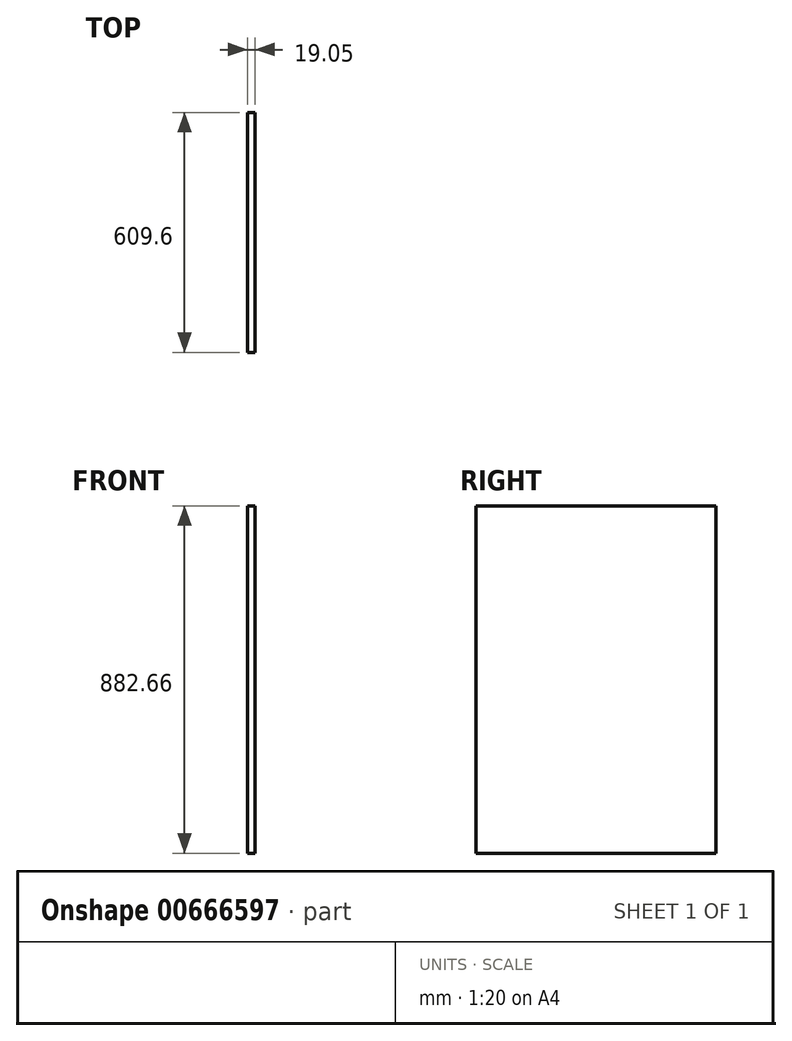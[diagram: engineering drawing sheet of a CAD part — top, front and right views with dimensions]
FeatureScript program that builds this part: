
annotation { "Feature Type Name" : "Feature", "Feature Type Description" : "" }
export const myFeature = defineFeature(function(context is Context, id is Id, definition is map)
    precondition{}
    {
        {
            var Q0;
            Q0=qCreatedBy(makeId("Right.planeOp"),FACE);
            var sketch = newSketch(context, id + "F0", { "sketchPlane" : qUnion([Q0])});
            skLineSegment(sketch, "E0.bottom", {"start": v(304.8, 441.32) * mm, "end": v(-304.8, 441.32) * mm});
            skLineSegment(sketch, "E0.top", {"start": v(304.8, -441.33) * mm, "end": v(-304.8, -441.33) * mm});
            skLineSegment(sketch, "E0.left", {"start": v(304.8, 441.33) * mm, "end": v(304.8, -441.33) * mm});
            skLineSegment(sketch, "E0.right", {"start": v(-304.8, 441.32) * mm, "end": v(-304.8, -441.33) * mm});
            skPoint(sketch, "E0.middle", {"position": v(0, 0) * mm});
            skSolve(sketch);
        }
        {
            var Q0;
            Q0=makeQuery(id+"F0.imprint","IMPRINT",FACE,{"disambiguationData":[TD([[makeQuery(id+"F0.imprint","IMPRINT",EDGE,{"derivedFrom":sQuery(id+"F0.wireOp",EDGE,"E0.bottom")}),1.0]])]});
            extrude(context, id + "F1", {"entities" : qUnion([Q0]), "depth" : 19.05 * mm, "offsetDistance" : 25.4 * mm});
        }
    });
